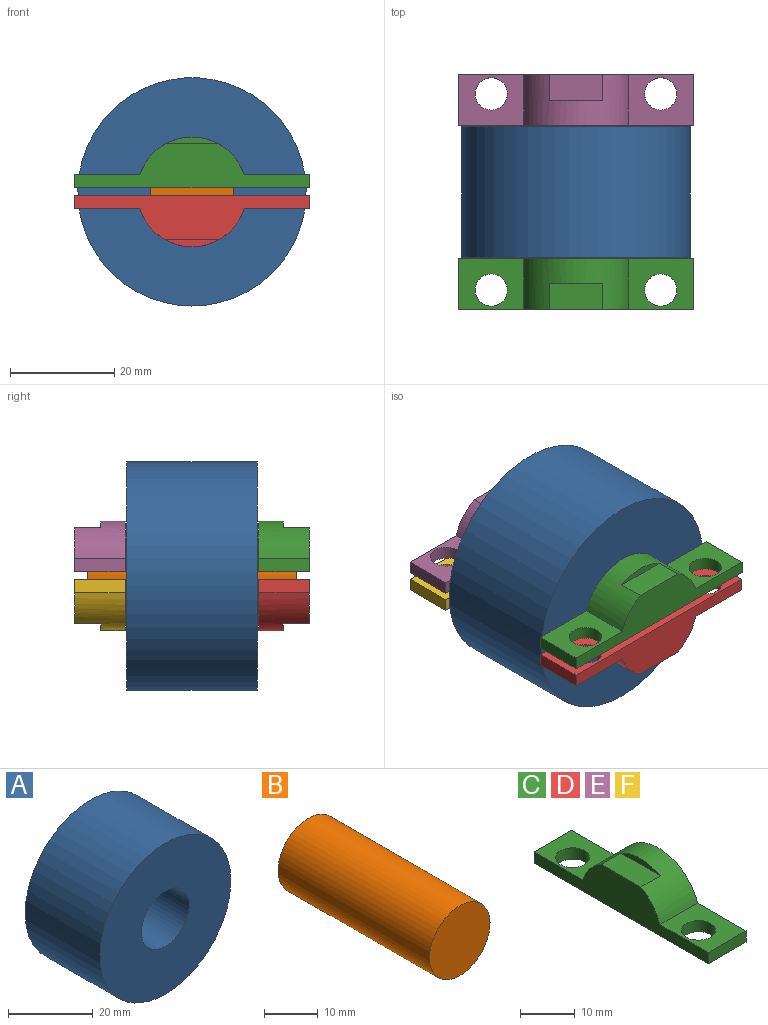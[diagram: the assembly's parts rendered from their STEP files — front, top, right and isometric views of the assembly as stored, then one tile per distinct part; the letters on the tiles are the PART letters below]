
ASSEMBLY  parts=6 mates=5
PART A: 4 faces, bbox 43.8x25x43.8 mm
  f0: cylinder r=8mm len=25mm, axis (0,1,0), area 1256.6mm2, adj f2,f3
  f1: cylinder r=21.88mm len=43.75mm, axis (0,1,0), area 3436.1mm2, adj f2,f3
  f2: plane 43.75x43.75mm, normal (0,-1,0), area 1302.2mm2, adj f0,f1
  f3: plane 43.75x43.75mm, normal (0,1,0), area 1302.2mm2, adj f0,f1
PART B: 3 faces, bbox 16x40x16 mm
  f0: cylinder r=8mm len=40mm, axis (0,1,0), area 2010.6mm2, adj f1,f2
  f1: plane 16x16mm, normal (0,-1,0), area 201.1mm2, adj f0
  f2: plane 16x16mm, normal (0,1,0), area 201.1mm2, adj f0
PART C: 14 faces, bbox 9.7x45x9.8 mm
  f0: cylinder r=10.5mm len=19.97mm, axis (-1,0,0), area 202.9mm2, adj f1,f4,f5,f8,f12,f13
  f1: plane 44.98x8.44mm, normal (-1,0,0), area 209.5mm2, adj f0,f3,f4,f5,f6,f7,f13
  f2: cylinder r=8mm len=15.93mm, axis (-1,0,0), area 170.1mm2, adj f7,f8,f9
  f3: plane 9.7x2.5mm, normal (0,1,0), area 24.2mm2, adj f1,f4,f7,f8
  f4: plane 12.5x9.7mm, normal (0,0,1), area 91.1mm2, adj f0,f1,f3,f8,f10
  f5: plane 12.5x9.7mm, normal (0,0,1), area 91.1mm2, adj f0,f1,f6,f8,f11
  f6: plane 9.7x2.5mm, normal (0,-1,0), area 24.2mm2, adj f1,f5,f7,f8
  f7: plane 44.98x9.7mm, normal (0,0,-1), area 261.2mm2, adj f1,f2,f3,f6,f8,f9,f10,f11
  f8: plane 44.98x9.75mm, normal (1,0,0), area 129.9mm2, adj f0,f2,f3,f4,f5,f6,f7
  f9: plane 15.93x7.25mm, normal (1,0,0), area 88.5mm2, adj f2,f7
  f10: cylinder r=3.1mm len=6.2mm, axis (0,0,1), area 48.7mm2, adj f4,f7
  f11: cylinder r=3.1mm len=6.2mm, axis (0,0,1), area 48.7mm2, adj f5,f7
  f12: plane 10.16x1.31mm, normal (-1,0,0), area 9mm2, adj f0,f13
  f13: plane 10.16x5mm, normal (0,0,1), area 50.8mm2, adj f0,f1,f12
PART D: same geometry as C
PART E: same geometry as C
PART F: same geometry as C
PLACE A t=(-26.98,-8,-7.39)mm
PLACE B t=(-26.98,-0.5,-7.39)mm
PLACE C rot(axis=(0,0,1),90deg) t=(-26.98,-40.5,-7.39)mm
PLACE D rot(axis=(0.71,0.71,0),180deg) t=(-26.98,-40.5,-7.39)mm
PLACE E rot(axis=(0,0,-1),90deg) t=(-26.98,-0.5,-7.39)mm
PLACE F rot(axis=(0.71,-0.71,0),180deg) t=(-26.98,-0.5,-7.39)mm
MATE fastened E.f2 <-> B.f0  axis (0,-1,0) through (-26.98,-0.5,-7.39)mm
MATE fastened D.f2 <-> B.f0  axis (0,1,0) through (-26.98,-40.5,-7.39)mm
MATE fastened B.f0 <-> A.f0  axis (0,1,0) through (-26.98,-20.5,-7.39)mm
MATE fastened F.f2 <-> B.f0  axis (0,-1,0) through (-26.98,-0.5,-7.39)mm
MATE fastened C.f2 <-> B.f0  axis (0,1,0) through (-26.98,-40.5,-7.39)mm
